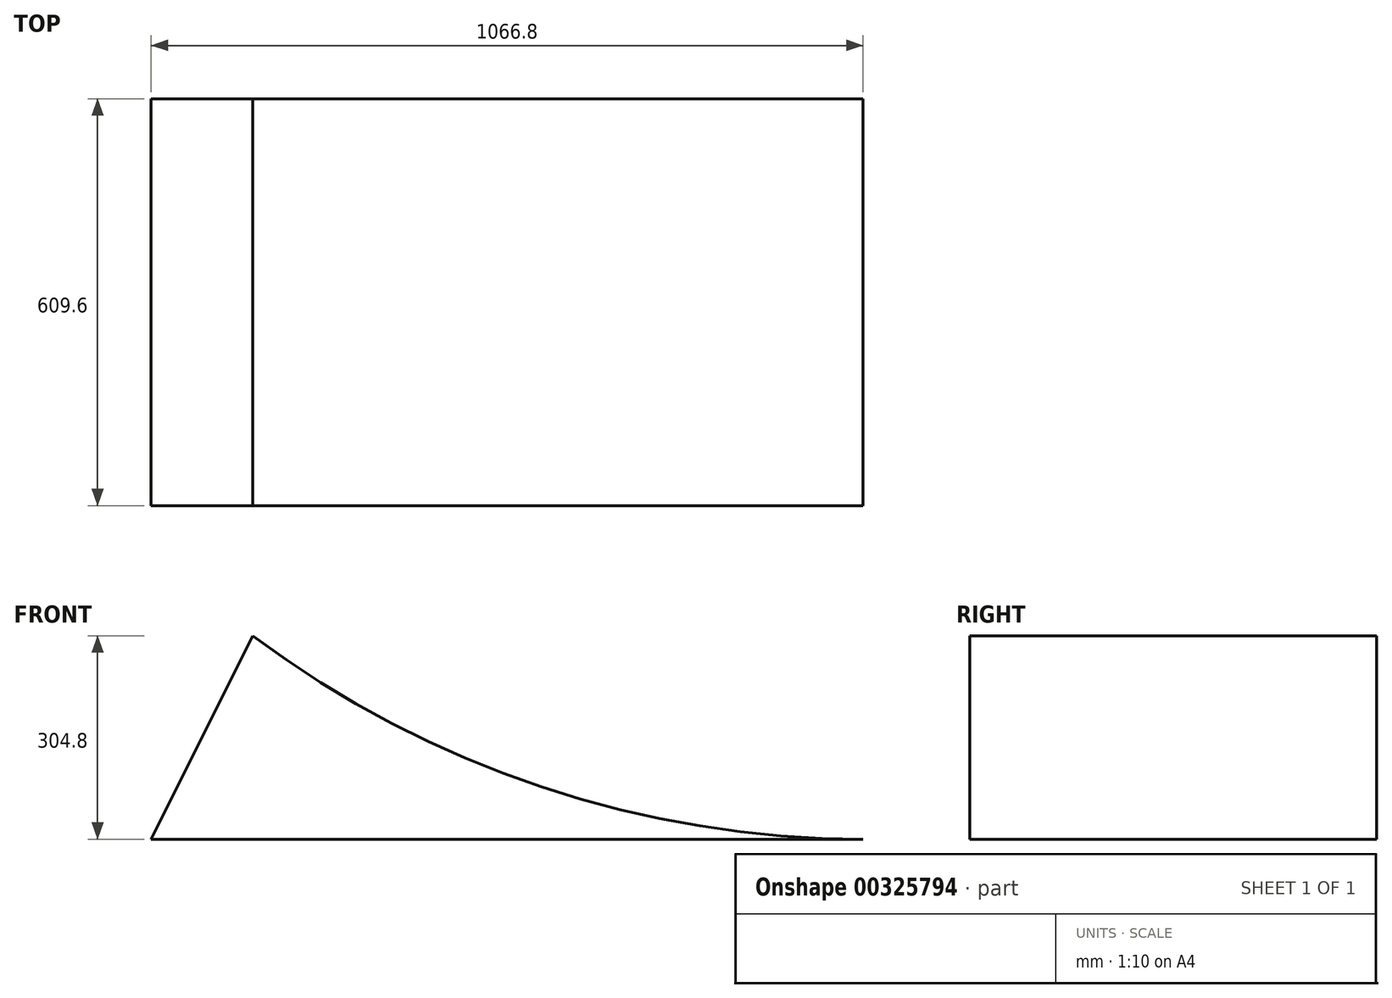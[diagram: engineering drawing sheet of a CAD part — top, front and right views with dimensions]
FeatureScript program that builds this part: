
annotation { "Feature Type Name" : "Feature", "Feature Type Description" : "" }
export const myFeature = defineFeature(function(context is Context, id is Id, definition is map)
    precondition{}
    {
        {
            var Q0;
            Q0=qCreatedBy(makeId("Front.planeOp"),FACE);
            var sketch = newSketch(context, id + "F0", { "sketchPlane" : qUnion([Q0])});
            skLineSegment(sketch, "E0.bottom", {"start": v(-533.4, 152.4) * mm, "end": v(533.4, 152.4) * mm});
            skLineSegment(sketch, "E0.top", {"start": v(-533.4, -152.4) * mm, "end": v(533.4, -152.4) * mm});
            skLineSegment(sketch, "E0.left", {"start": v(-533.4, 152.4) * mm, "end": v(-533.4, -152.4) * mm});
            skLineSegment(sketch, "E0.right", {"start": v(533.4, 152.4) * mm, "end": v(533.4, -152.4) * mm});
            skPoint(sketch, "E0.middle", {"position": v(0, 0) * mm});
            skLineSegment(sketch, "E1", {"start": v(-381, 152.4) * mm, "end": v(-381, -152.4) * mm, "construction": true});
            skLineSegment(sketch, "E2", {"start": v(-381, 152.4) * mm, "end": v(-533.4, -152.4) * mm});
            skArc(sketch, "E3", {"start": v(-381, 152.4) * mm, "mid": v(51.47, -74.2) * mm, "end": v(533.4, -152.4) * mm});
            skSolve(sketch);
        }
        {
            var Q0;
            Q0=makeQuery(id+"F0.imprint","IMPRINT",FACE,{"disambiguationData":[TD([[makeQuery(id+"F0.imprint","IMPRINT",EDGE,{"derivedFrom":sQuery(id+"F0.wireOp",EDGE,"E0.top")}),1.0]])]});
            extrude(context, id + "F1", {"entities" : qUnion([Q0]), "endBound" : BoundingType.SYMMETRIC, "depth" : 609.6 * mm});
        }
    });
